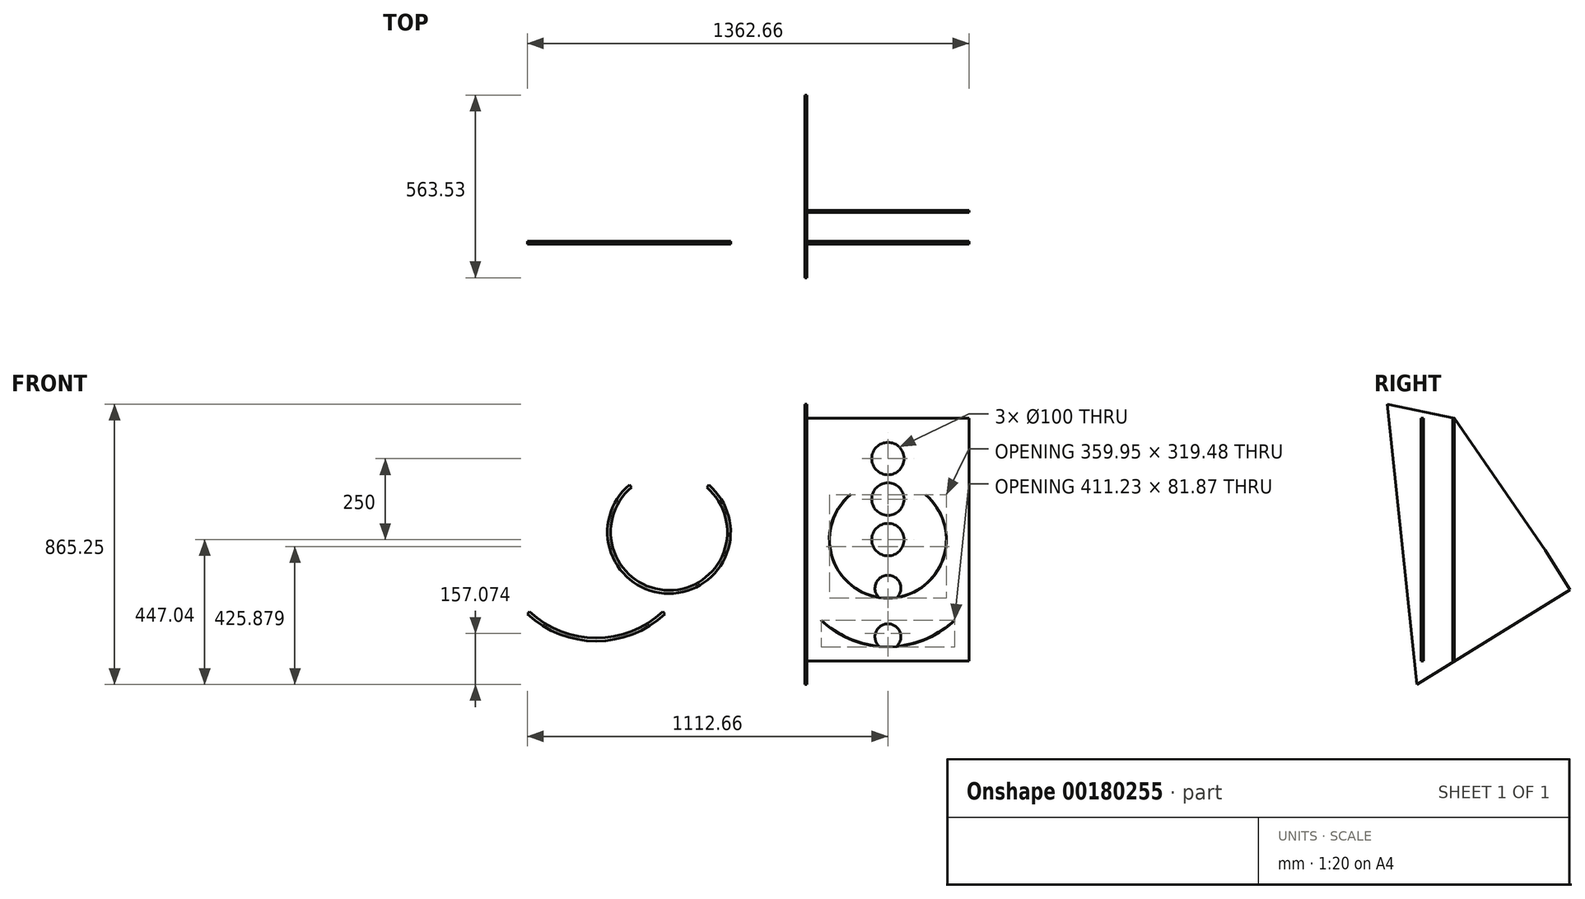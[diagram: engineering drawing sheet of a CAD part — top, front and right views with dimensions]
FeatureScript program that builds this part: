
annotation { "Feature Type Name" : "Feature", "Feature Type Description" : "" }
export const myFeature = defineFeature(function(context is Context, id is Id, definition is map)
    precondition{}
    {
        {
            var Q0;
            Q0=qCreatedBy(makeId("Front.planeOp"),FACE);
            var sketch = newSketch(context, id + "F0", { "sketchPlane" : qUnion([Q0])});
            skArc(sketch, "E0", {"start": v(28.89, -177.67) * mm, "mid": v(0, -110) * mm, "end": v(-28.89, -177.67) * mm});
            skLineSegment(sketch, "E1", {"start": v(0, -300) * mm, "end": v(0, 0) * mm, "construction": true});
            skCircle(sketch, "E2", {"center": v(0, 125) * mm, "radius": 50 * mm});
            skCircle(sketch, "E3", {"center": v(0, 250) * mm, "radius": 50 * mm});
            skArc(sketch, "E4", {"start": v(27.86, -328.7) * mm, "mid": v(0, -260) * mm, "end": v(-27.86, -328.7) * mm});
            skCircle(sketch, "E5", {"center": v(0, 0) * mm, "radius": 50 * mm});
            skArc(sketch, "E6", {"start": v(-115.7, 137.89) * mm, "mid": v(0, -180) * mm, "end": v(115.7, 137.89) * mm});
            skLineSegment(sketch, "E7.bottom", {"start": v(-250, 375) * mm, "end": v(250, 375) * mm});
            skLineSegment(sketch, "E7.top", {"start": v(-250, -375) * mm, "end": v(250, -375) * mm});
            skLineSegment(sketch, "E7.left", {"start": v(-250, 375) * mm, "end": v(-250, -375) * mm});
            skLineSegment(sketch, "E7.right", {"start": v(250, 375) * mm, "end": v(250, -375) * mm});
            skArc(sketch, "E8", {"start": v(-205, -249.03) * mm, "mid": v(0, -330) * mm, "end": v(205, -249.03) * mm});
            skPoint(sketch, "E9", {"position": v(0, -110) * mm});
            skLineSegment(sketch, "E10", {"start": v(0, 0) * mm, "end": v(-158.36, 188.73) * mm, "construction": true});
            skLineSegment(sketch, "E11", {"start": v(0, 0) * mm, "end": v(0, 436.66) * mm, "construction": true});
            skPoint(sketch, "E11.endSnap0", {"position": v(0, 375) * mm});
            skLineSegment(sketch, "E12.MirrorCS", {"start": v(0, 0) * mm, "end": v(158.36, 188.73) * mm, "construction": true});
            skArc(sketch, "E13.0", {"start": v(-116.28, 138.58) * mm, "mid": v(0, -180.9) * mm, "end": v(116.28, 138.58) * mm});
            skLineSegment(sketch, "E14", {"start": v(-205, -170.57) * mm, "end": v(-205, -331.82) * mm, "construction": true});
            skLineSegment(sketch, "E15.MirrorCS", {"start": v(205, -170.57) * mm, "end": v(205, -331.82) * mm, "construction": true});
            skArc(sketch, "E16.0", {"start": v(-205.62, -249.69) * mm, "mid": v(0, -330.9) * mm, "end": v(205.61, -249.69) * mm});
            skLineSegment(sketch, "E17", {"start": v(-205, -249.03) * mm, "end": v(-205.62, -249.69) * mm});
            skLineSegment(sketch, "E18", {"start": v(205, -249.03) * mm, "end": v(205.61, -249.69) * mm});
            skLineSegment(sketch, "E19", {"start": v(116.28, 138.58) * mm, "end": v(115.7, 137.89) * mm});
            skLineSegment(sketch, "E20", {"start": v(-116.28, 138.58) * mm, "end": v(-115.7, 137.89) * mm});
            skArc(sketch, "E21", {"start": v(-791.14, 161.34) * mm, "mid": v(-675.97, -156.55) * mm, "end": v(-558.93, 160.65) * mm});
            skArc(sketch, "E22.0", {"start": v(-797.57, 169) * mm, "mid": v(-676, -166.55) * mm, "end": v(-552.46, 168.28) * mm});
            skLineSegment(sketch, "E23", {"start": v(-797.57, 169) * mm, "end": v(-791.14, 161.34) * mm});
            skLineSegment(sketch, "E24", {"start": v(-558.93, 160.65) * mm, "end": v(-552.46, 168.28) * mm});
            skArc(sketch, "E25.0", {"start": v(-1105.82, -221.96) * mm, "mid": v(-900.2, -303.17) * mm, "end": v(-694.6, -221.96) * mm});
            skArc(sketch, "E26.0", {"start": v(-1112.66, -229.26) * mm, "mid": v(-900.2, -313.17) * mm, "end": v(-687.76, -229.26) * mm});
            skLineSegment(sketch, "E27", {"start": v(-1112.66, -229.26) * mm, "end": v(-1105.82, -221.96) * mm});
            skLineSegment(sketch, "E28", {"start": v(-694.6, -221.96) * mm, "end": v(-687.76, -229.26) * mm});
            skSolve(sketch);
        }
        {
            var Q0;
            Q0 = qSketchRegion(id + "F0", true);
            extrude(context, id + "F1", {"entities" : qUnion([Q0]), "depth" : 8 * mm});
        }
        {
            var Q0;
            Q0=makeQuery(id+"F1.opExtrude","CAP_FACE",FACE,{"disambiguationData":[OSD([sQuery(id+"F0.wireOp",EDGE,"E0"),sQuery(id+"F0.wireOp",EDGE,"E2"),sQuery(id+"F0.wireOp",EDGE,"E3"),sQuery(id+"F0.wireOp",EDGE,"E4"),sQuery(id+"F0.wireOp",EDGE,"E5"),sQuery(id+"F0.wireOp",EDGE,"E6"),sQuery(id+"F0.wireOp",EDGE,"E7.bottom"),sQuery(id+"F0.wireOp",EDGE,"E7.top"),sQuery(id+"F0.wireOp",EDGE,"E7.left"),sQuery(id+"F0.wireOp",EDGE,"E7.right"),sQuery(id+"F0.wireOp",EDGE,"E8"),sQuery(id+"F0.wireOp",EDGE,"E13.0"),sQuery(id+"F0.wireOp",EDGE,"E16.0"),sQuery(id+"F0.wireOp",EDGE,"E17"),sQuery(id+"F0.wireOp",EDGE,"E18"),sQuery(id+"F0.wireOp",EDGE,"E19"),sQuery(id+"F0.wireOp",EDGE,"E20")])],"isStart":true});
            cPlane(context, id + "F2", {"entities" : qUnion([Q0]), "cplaneType" : CPlaneType.OFFSET, "offset" : 90 * mm, "width" : 150 * mm, "height" : 150 * mm});
        }
        {
            var Q0;
            Q0=qCreatedBy(id+"F2.planeOp",FACE);
            var sketch = newSketch(context, id + "F3", { "sketchPlane" : qUnion([Q0])});
            skLineSegment(sketch, "E29.0", {"start": v(-250, 375) * mm, "end": v(-250, -375) * mm});
            skLineSegment(sketch, "E29.1", {"start": v(250, -375) * mm, "end": v(-250, -375) * mm});
            skLineSegment(sketch, "E29.2", {"start": v(250, 375) * mm, "end": v(250, -375) * mm});
            skLineSegment(sketch, "E29.3", {"start": v(250, 375) * mm, "end": v(-250, 375) * mm});
            skSolve(sketch);
        }
        {
            var Q0;
            Q0 = qSketchRegion(id + "F3", true);
            extrude(context, id + "F4", {"entities" : qUnion([Q0]), "depth" : 6 * mm});
        }
        {
            var Q0;
            Q0=makeQuery(id+"F1.opExtrude","SWEPT_FACE",FACE,{"disambiguationData":[OSD([sQuery(id+"F0.wireOp",EDGE,"E7.left")])]});
            var sketch = newSketch(context, id + "F5", { "sketchPlane" : qUnion([Q0])});
            skLineSegment(sketch, "E30", {"start": v(20.14, -447.04) * mm, "end": v(-451.63, -154.42) * mm});
            skLineSegment(sketch, "E31", {"start": v(-451.63, -154.42) * mm, "end": v(-376.02, -32.5) * mm});
            skLineSegment(sketch, "E32", {"start": v(-376.02, -32.5) * mm, "end": v(-96, 375) * mm});
            skLineSegment(sketch, "E33", {"start": v(-96, 375) * mm, "end": v(111.9, 418.2) * mm});
            skPoint(sketch, "E34.0", {"position": v(-96, 375) * mm});
            skLineSegment(sketch, "E35", {"start": v(111.9, 418.2) * mm, "end": v(20.14, -447.04) * mm});
            skSolve(sketch);
        }
        {
            var Q0;
            Q0 = qSketchRegion(id + "F5", true);
            extrude(context, id + "F6", {"entities" : qUnion([Q0]), "depth" : 6 * mm});
        }
        {
            var Q0;
            Q0=makeQuery(id+"F1.opExtrude","CAP_FACE",FACE,{"disambiguationData":[OSD([sQuery(id+"F0.wireOp",EDGE,"E0"),sQuery(id+"F0.wireOp",EDGE,"E2"),sQuery(id+"F0.wireOp",EDGE,"E3"),sQuery(id+"F0.wireOp",EDGE,"E4"),sQuery(id+"F0.wireOp",EDGE,"E5"),sQuery(id+"F0.wireOp",EDGE,"E6"),sQuery(id+"F0.wireOp",EDGE,"E7.bottom"),sQuery(id+"F0.wireOp",EDGE,"E7.top"),sQuery(id+"F0.wireOp",EDGE,"E7.left"),sQuery(id+"F0.wireOp",EDGE,"E7.right"),sQuery(id+"F0.wireOp",EDGE,"E8"),sQuery(id+"F0.wireOp",EDGE,"E13.0"),sQuery(id+"F0.wireOp",EDGE,"E16.0"),sQuery(id+"F0.wireOp",EDGE,"E17"),sQuery(id+"F0.wireOp",EDGE,"E18"),sQuery(id+"F0.wireOp",EDGE,"E19"),sQuery(id+"F0.wireOp",EDGE,"E20")])],"isStart":false});
            var sketch = newSketch(context, id + "F7", { "sketchPlane" : qUnion([Q0])});
            skLineSegment(sketch, "E36.bottom", {"start": v(57.35, -195.15) * mm, "end": v(66.02, -195.15) * mm});
            skLineSegment(sketch, "E36.top", {"start": v(57.35, -205.26) * mm, "end": v(66.02, -205.26) * mm});
            skLineSegment(sketch, "E36.left", {"start": v(57.35, -195.15) * mm, "end": v(57.35, -205.26) * mm});
            skLineSegment(sketch, "E36.right", {"start": v(66.02, -195.15) * mm, "end": v(66.02, -205.26) * mm});
            skLineSegment(sketch, "E37.bottom", {"start": v(-233.72, -229.82) * mm, "end": v(-223.6, -229.82) * mm});
            skLineSegment(sketch, "E37.top", {"start": v(-233.72, -237.77) * mm, "end": v(-223.6, -237.77) * mm});
            skLineSegment(sketch, "E37.left", {"start": v(-233.72, -229.82) * mm, "end": v(-233.72, -237.77) * mm});
            skLineSegment(sketch, "E37.right", {"start": v(-223.6, -229.82) * mm, "end": v(-223.6, -237.77) * mm});
            skLineSegment(sketch, "E38.bottom", {"start": v(-116.28, -216.82) * mm, "end": v(-105.88, -216.82) * mm});
            skLineSegment(sketch, "E38.top", {"start": v(-116.28, -226.93) * mm, "end": v(-105.88, -226.93) * mm});
            skLineSegment(sketch, "E38.left", {"start": v(-116.28, -216.82) * mm, "end": v(-116.28, -226.93) * mm});
            skLineSegment(sketch, "E38.right", {"start": v(-105.88, -216.82) * mm, "end": v(-105.88, -226.93) * mm});
            skSolve(sketch);
        }
        {
            var Q0;
            Q0 = qSketchRegion(id + "F7", true);
            extrude(context, id + "F8", {"entities" : qUnion([Q0]), "oppositeDirection" : true, "depth" : 120 * mm});
        }
        {
            var Q0;
            Q0=makeQuery(id+"F8.opExtrude","SWEPT_BODY",BODY,{"disambiguationData":[OSD([sQuery(id+"F7.wireOp",EDGE,"E38.bottom"),sQuery(id+"F7.wireOp",EDGE,"E38.top"),sQuery(id+"F7.wireOp",EDGE,"E38.left"),sQuery(id+"F7.wireOp",EDGE,"E38.right")])]});
            deleteBodies(context, id + "F9", {"entities" : qUnion([Q0])});
        }
        {
            var Q0;
            Q0=makeQuery(id+"F8.opExtrude","SWEPT_BODY",BODY,{"disambiguationData":[OSD([sQuery(id+"F7.wireOp",EDGE,"E37.bottom"),sQuery(id+"F7.wireOp",EDGE,"E37.top"),sQuery(id+"F7.wireOp",EDGE,"E37.left"),sQuery(id+"F7.wireOp",EDGE,"E37.right")])]});
            var Q1;
            Q1=makeQuery(id+"F8.opExtrude","SWEPT_BODY",BODY,{"disambiguationData":[OSD([sQuery(id+"F7.wireOp",EDGE,"E36.bottom"),sQuery(id+"F7.wireOp",EDGE,"E36.top"),sQuery(id+"F7.wireOp",EDGE,"E36.left"),sQuery(id+"F7.wireOp",EDGE,"E36.right")])]});
            deleteBodies(context, id + "F10", {"entities" : qUnion([Q0, Q1])});
        }
    });
